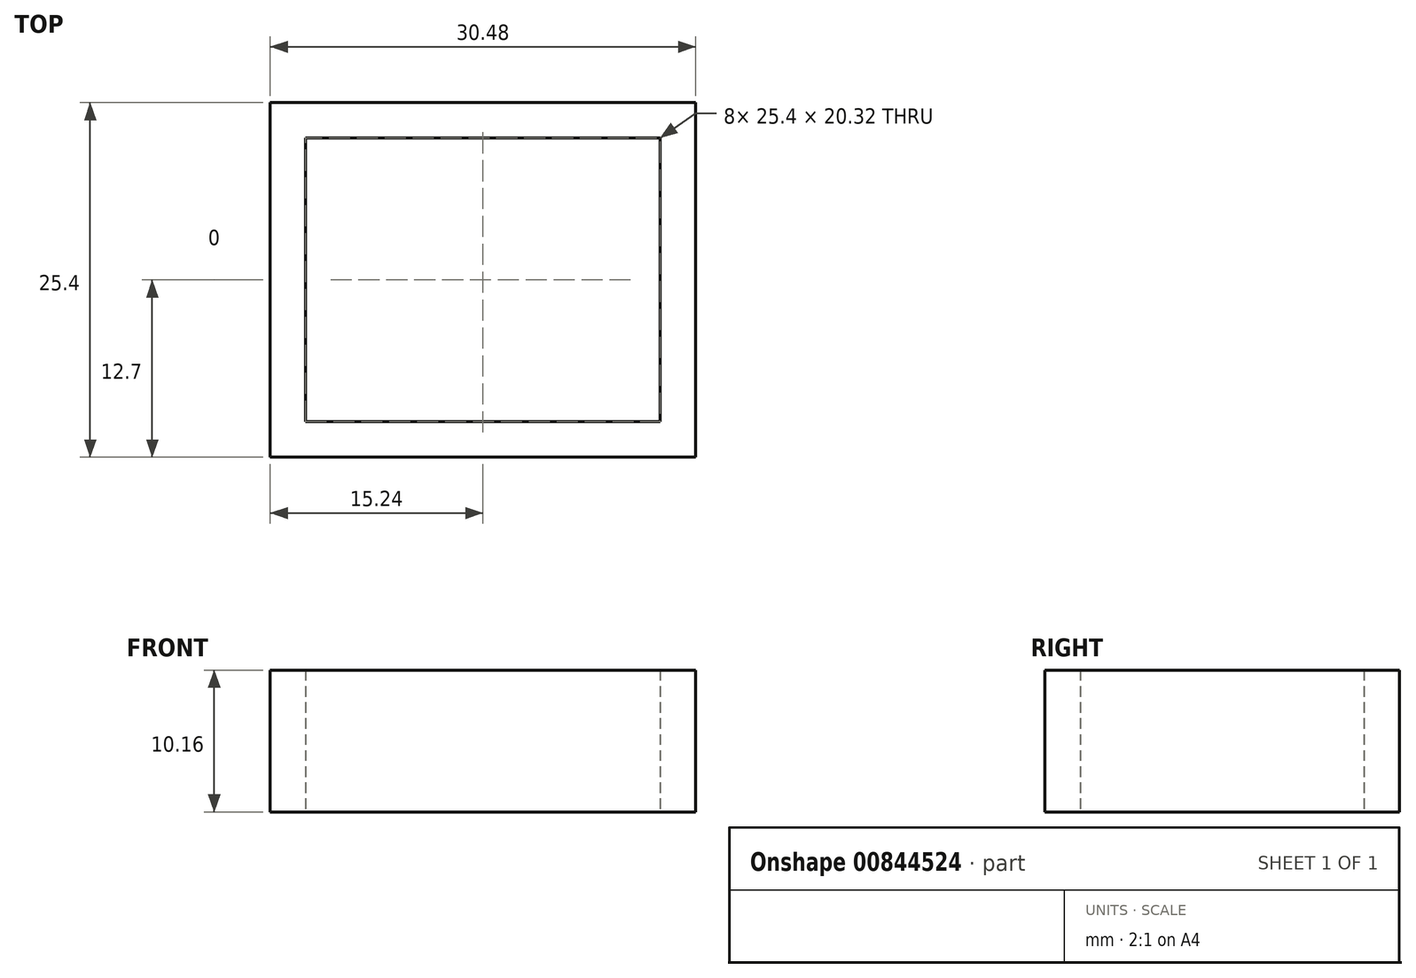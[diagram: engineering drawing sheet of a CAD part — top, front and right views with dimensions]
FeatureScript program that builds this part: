
annotation { "Feature Type Name" : "Feature", "Feature Type Description" : "" }
export const myFeature = defineFeature(function(context is Context, id is Id, definition is map)
    precondition{}
    {
        {
            var Q0;
            Q0=qCreatedBy(makeId("Top.planeOp"),FACE);
            var sketch = newSketch(context, id + "F0", { "sketchPlane" : qUnion([Q0])});
            skLineSegment(sketch, "E0.bottom", {"start": v(-15.24, 12.7) * mm, "end": v(15.24, 12.7) * mm});
            skLineSegment(sketch, "E0.top", {"start": v(-15.24, -12.7) * mm, "end": v(15.24, -12.7) * mm});
            skLineSegment(sketch, "E0.left", {"start": v(-15.24, 12.7) * mm, "end": v(-15.24, -12.7) * mm});
            skLineSegment(sketch, "E0.right", {"start": v(15.24, 12.7) * mm, "end": v(15.24, -12.7) * mm});
            skPoint(sketch, "E0.middle", {"position": v(0, 0) * mm});
            skCircle(sketch, "E1", {"center": v(-6.35, 0) * mm, "radius": 2.16 * mm});
            skCircle(sketch, "E2", {"center": v(6.35, 0) * mm, "radius": 2.16 * mm});
            skLineSegment(sketch, "E3.bottom", {"start": v(-12.7, 10.16) * mm, "end": v(12.7, 10.16) * mm});
            skLineSegment(sketch, "E3.top", {"start": v(-12.7, -10.16) * mm, "end": v(12.7, -10.16) * mm});
            skLineSegment(sketch, "E3.left", {"start": v(-12.7, 10.16) * mm, "end": v(-12.7, -10.16) * mm});
            skLineSegment(sketch, "E3.right", {"start": v(12.7, 10.16) * mm, "end": v(12.7, -10.16) * mm});
            skSolve(sketch);
        }
        {
            var Q0;
            Q0=qSketchRegion(id+"F0",true);
            extrude(context, id + "F1", {"entities" : qUnion([Q0]), "endBound" : BoundingType.SYMMETRIC, "depth" : 10.16 * mm, "offsetDistance" : 25.4 * mm});
        }
    });
